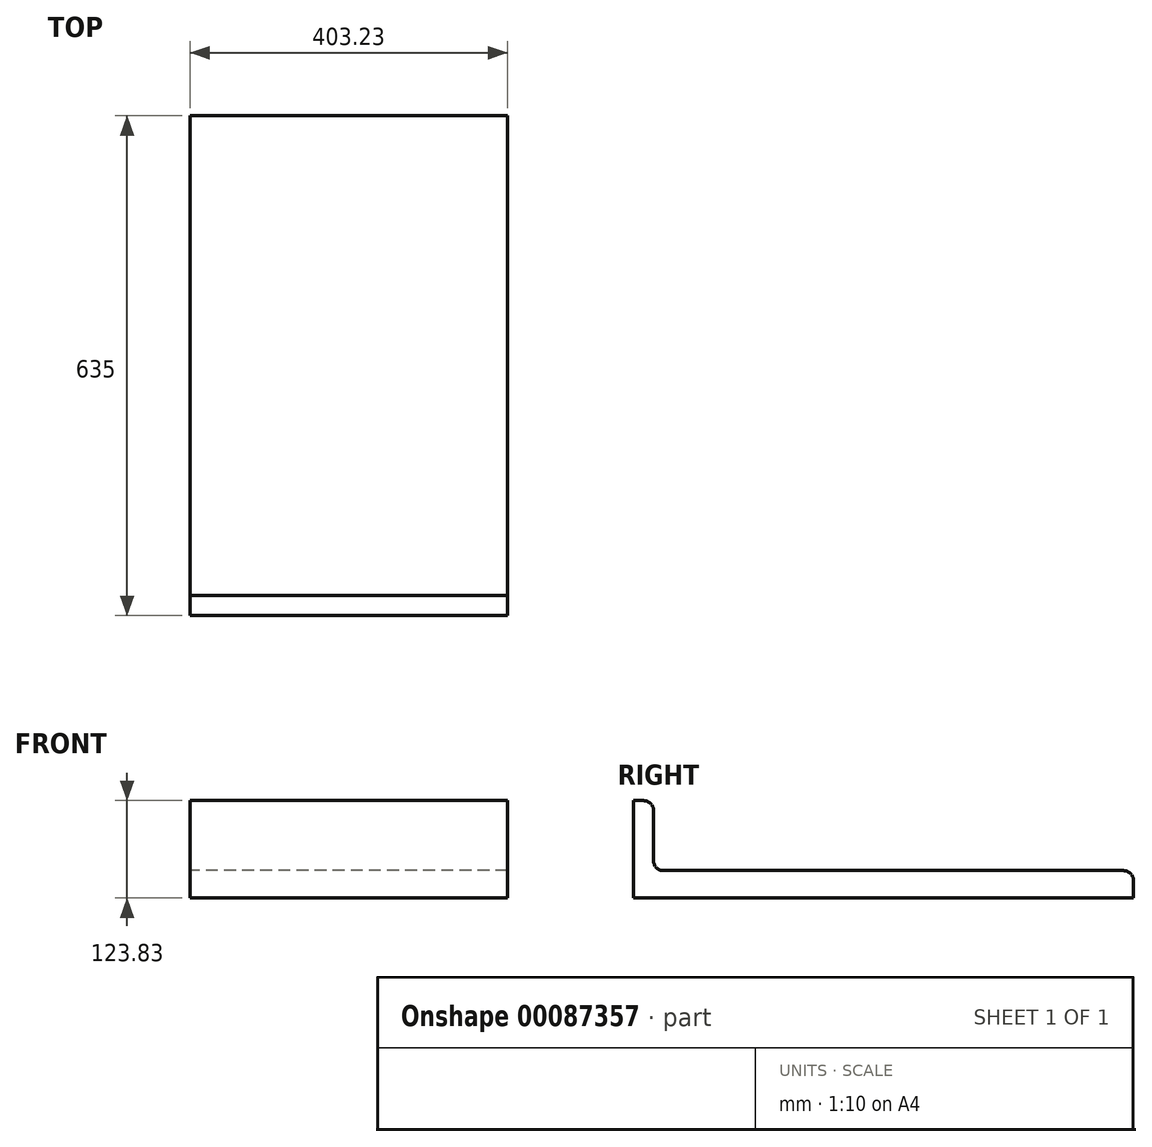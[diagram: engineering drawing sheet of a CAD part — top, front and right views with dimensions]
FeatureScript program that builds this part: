
annotation { "Feature Type Name" : "Feature", "Feature Type Description" : "" }
export const myFeature = defineFeature(function(context is Context, id is Id, definition is map)
    precondition{}
    {
        {
            var Q0;
            Q0=qCreatedBy(makeId("Right.planeOp"),FACE);
            var sketch = newSketch(context, id + "F0", { "sketchPlane" : qUnion([Q0])});
            skLineSegment(sketch, "E0.bottom", {"start": v(0, 0) * mm, "end": v(635, 0) * mm});
            skLineSegment(sketch, "E0.right", {"start": v(635, 0) * mm, "end": v(635, 22.23) * mm});
            skLineSegment(sketch, "E1.top", {"start": v(0, 123.83) * mm, "end": v(12.7, 123.83) * mm});
            skLineSegment(sketch, "E1.right", {"start": v(25.4, 47.62) * mm, "end": v(25.4, 111.13) * mm});
            skPoint(sketch, "E2.visualSharp", {"position": v(25.4, 123.83) * mm});
            skArc(sketch, "E2.filletArc", {"start": v(25.4, 111.13) * mm, "mid": v(21.68, 120.1) * mm, "end": v(12.7, 123.83) * mm});
            skLineSegment(sketch, "E3", {"start": v(622.3, 34.93) * mm, "end": v(38.1, 34.92) * mm});
            skPoint(sketch, "E4.visualSharp", {"position": v(25.4, 34.92) * mm});
            skArc(sketch, "E4.filletArc", {"start": v(25.4, 47.62) * mm, "mid": v(29.12, 38.64) * mm, "end": v(38.1, 34.92) * mm});
            skPoint(sketch, "E5.visualSharp", {"position": v(635, 34.93) * mm});
            skArc(sketch, "E5.filletArc", {"start": v(635, 22.23) * mm, "mid": v(631.28, 31.2) * mm, "end": v(622.3, 34.93) * mm});
            skLineSegment(sketch, "E6", {"start": v(0, 123.83) * mm, "end": v(0, 0) * mm});
            skSolve(sketch);
        }
        {
            var Q0;
            Q0=makeQuery(id+"F0.imprint","IMPRINT",FACE,{"disambiguationData":[TD([[makeQuery(id+"F0.imprint","IMPRINT",EDGE,{"derivedFrom":sQuery(id+"F0.wireOp",EDGE,"E0.bottom")}),1.0]])]});
            extrude(context, id + "F1", {"entities" : qUnion([Q0]), "depth" : 403.22 * mm});
        }
    });
